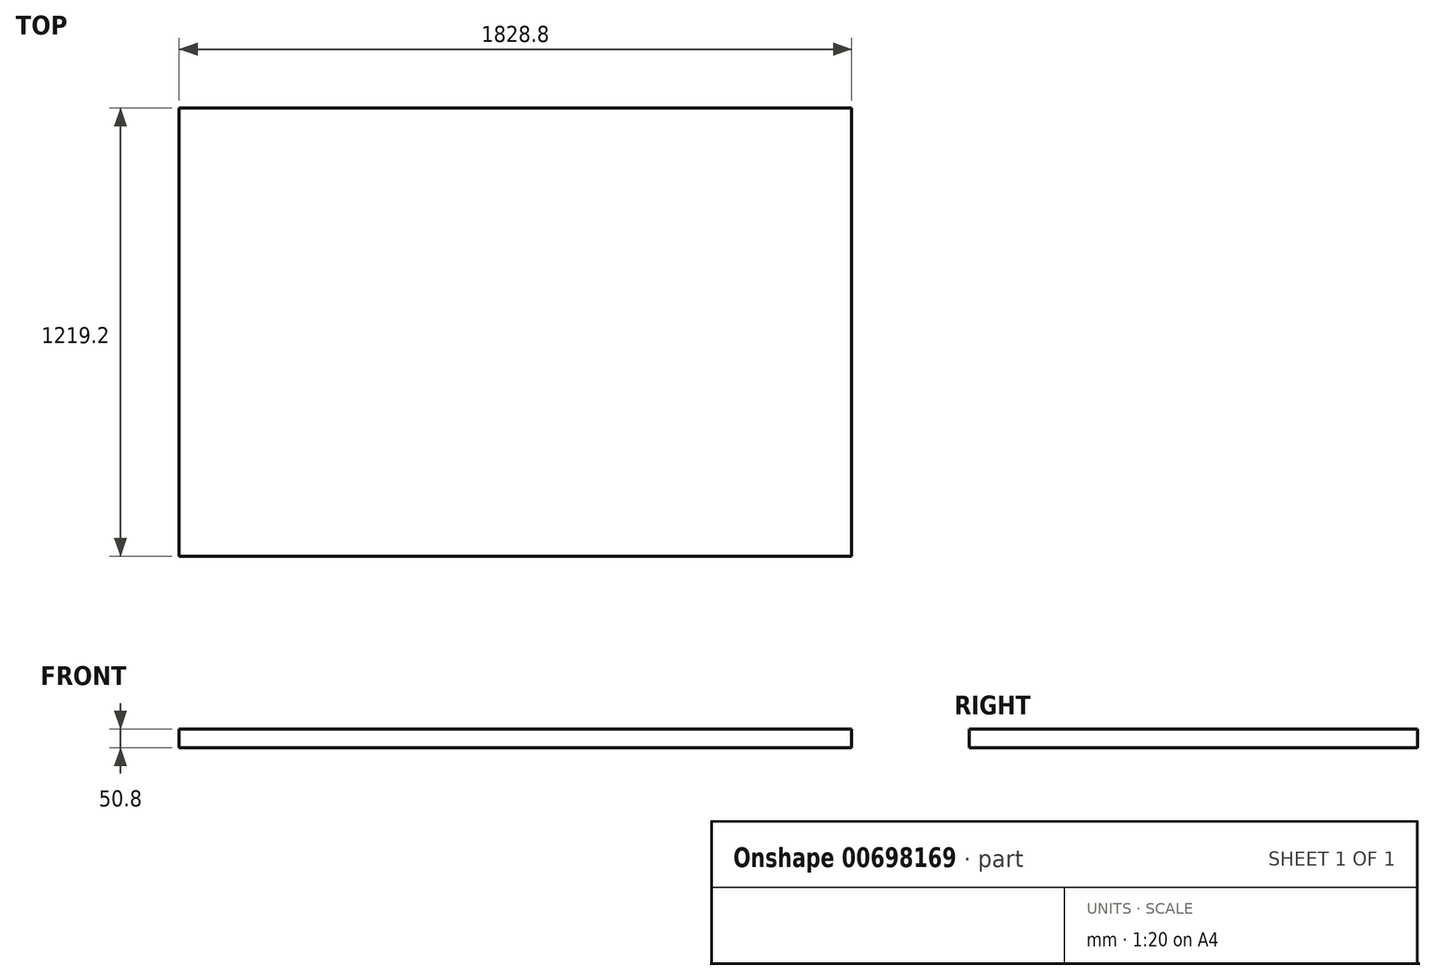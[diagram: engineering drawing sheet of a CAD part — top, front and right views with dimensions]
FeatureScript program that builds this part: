
annotation { "Feature Type Name" : "Feature", "Feature Type Description" : "" }
export const myFeature = defineFeature(function(context is Context, id is Id, definition is map)
    precondition{}
    {
        {
            var Q0;
            Q0=qCreatedBy(makeId("Top.planeOp"),FACE);
            var sketch = newSketch(context, id + "F0", { "sketchPlane" : qUnion([Q0])});
            skLineSegment(sketch, "E0.bottom", {"start": v(-914.4, 609.6) * mm, "end": v(914.4, 609.6) * mm});
            skLineSegment(sketch, "E0.top", {"start": v(-914.4, -609.6) * mm, "end": v(914.4, -609.6) * mm});
            skLineSegment(sketch, "E0.left", {"start": v(-914.4, 609.6) * mm, "end": v(-914.4, -609.6) * mm});
            skLineSegment(sketch, "E0.right", {"start": v(914.4, 609.6) * mm, "end": v(914.4, -609.6) * mm});
            skPoint(sketch, "E0.middle", {"position": v(0, 0) * mm});
            skSolve(sketch);
        }
        {
            var Q0;
            Q0=makeQuery(id+"F0.imprint","IMPRINT",FACE,{"disambiguationData":[TD([[makeQuery(id+"F0.imprint","IMPRINT",EDGE,{"derivedFrom":sQuery(id+"F0.wireOp",EDGE,"E0.bottom")}),-1.0]])]});
            extrude(context, id + "F1", {"entities" : qUnion([Q0]), "depth" : 50.8 * mm, "offsetDistance" : 25.4 * mm});
        }
    });
